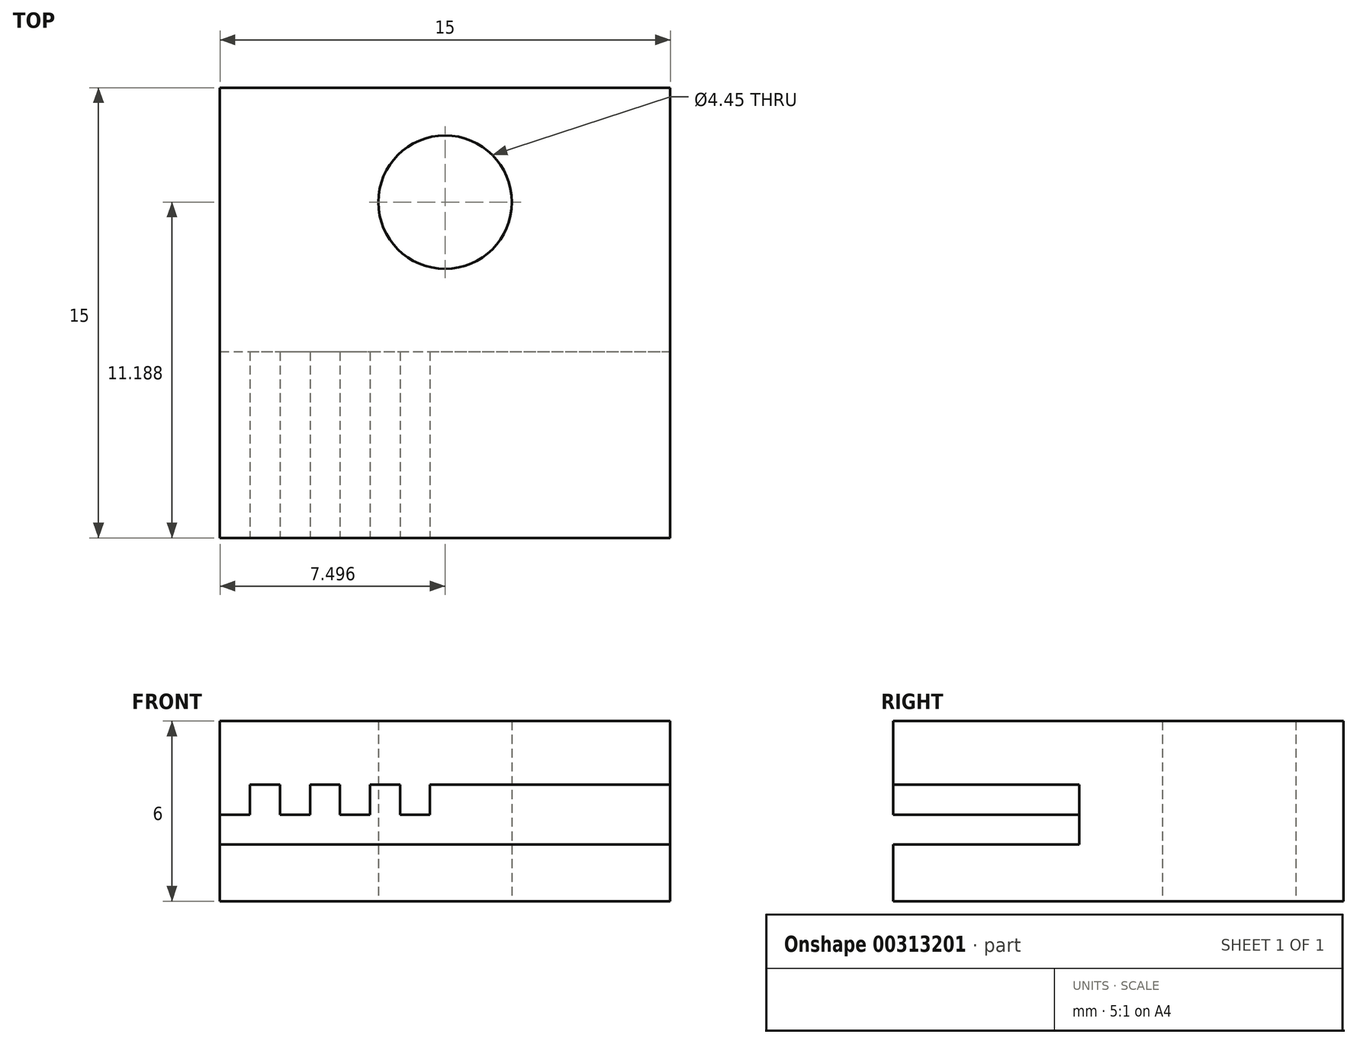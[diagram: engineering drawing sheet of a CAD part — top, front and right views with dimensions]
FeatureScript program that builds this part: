
annotation { "Feature Type Name" : "Feature", "Feature Type Description" : "" }
export const myFeature = defineFeature(function(context is Context, id is Id, definition is map)
    precondition{}
    {
        {
            var Q0;
            Q0=qCreatedBy(makeId("Top.planeOp"),FACE);
            var sketch = newSketch(context, id + "F0", { "sketchPlane" : qUnion([Q0])});
            skLineSegment(sketch, "E0.bottom", {"start": v(6.14, 10.11) * mm, "end": v(21.14, 10.11) * mm});
            skLineSegment(sketch, "E0.top", {"start": v(6.14, -4.89) * mm, "end": v(21.14, -4.89) * mm});
            skLineSegment(sketch, "E0.left", {"start": v(6.14, 10.11) * mm, "end": v(6.14, -4.89) * mm});
            skLineSegment(sketch, "E0.right", {"start": v(21.14, 10.11) * mm, "end": v(21.14, -4.89) * mm});
            skSolve(sketch);
        }
        {
            var Q0;
            Q0=qSketchRegion(id+"F0",true);
            extrude(context, id + "F1", {"entities" : qUnion([Q0]), "depth" : 6 * mm});
        }
        {
            var Q0;
            Q0=makeQuery(id+"F1.opExtrude","SWEPT_FACE",FACE,{"disambiguationData":[OSD([sQuery(id+"F0.wireOp",EDGE,"E0.top")])]});
            var sketch = newSketch(context, id + "F2", { "sketchPlane" : qUnion([Q0])});
            skLineSegment(sketch, "E1", {"start": v(6.14, 1.88) * mm, "end": v(21.14, 1.88) * mm});
            skLineSegment(sketch, "E2", {"start": v(6.14, 2.88) * mm, "end": v(7.14, 2.88) * mm});
            skLineSegment(sketch, "E3", {"start": v(7.14, 2.88) * mm, "end": v(7.14, 3.88) * mm});
            skLineSegment(sketch, "E4", {"start": v(7.14, 3.88) * mm, "end": v(8.14, 3.88) * mm});
            skLineSegment(sketch, "E5", {"start": v(8.14, 3.88) * mm, "end": v(8.14, 2.88) * mm});
            skLineSegment(sketch, "E6.1.0.0", {"start": v(10.14, 3.88) * mm, "end": v(10.14, 2.88) * mm});
            skLineSegment(sketch, "E6.1.0.1", {"start": v(9.14, 3.88) * mm, "end": v(10.14, 3.88) * mm});
            skLineSegment(sketch, "E6.1.0.2", {"start": v(9.14, 2.88) * mm, "end": v(9.14, 3.88) * mm});
            skLineSegment(sketch, "E6.1.0.3", {"start": v(8.14, 2.88) * mm, "end": v(9.14, 2.88) * mm});
            skLineSegment(sketch, "E6.2.0.0", {"start": v(12.14, 3.88) * mm, "end": v(12.14, 2.88) * mm});
            skLineSegment(sketch, "E6.2.0.1", {"start": v(11.14, 3.88) * mm, "end": v(12.14, 3.88) * mm});
            skLineSegment(sketch, "E6.2.0.2", {"start": v(11.14, 2.88) * mm, "end": v(11.14, 3.88) * mm});
            skLineSegment(sketch, "E6.2.0.3", {"start": v(10.14, 2.88) * mm, "end": v(11.14, 2.88) * mm});
            skLineSegment(sketch, "E6.3.0.1", {"start": v(13.14, 3.88) * mm, "end": v(14.14, 3.88) * mm});
            skLineSegment(sketch, "E6.3.0.2", {"start": v(13.14, 2.88) * mm, "end": v(13.14, 3.88) * mm});
            skLineSegment(sketch, "E6.3.0.3", {"start": v(12.14, 2.88) * mm, "end": v(13.14, 2.88) * mm});
            skLineSegment(sketch, "E6.direction1", {"start": v(6.14, 2.88) * mm, "end": v(8.14, 2.88) * mm, "construction": true});
            skLineSegment(sketch, "E7", {"start": v(14.14, 3.88) * mm, "end": v(21.14, 3.88) * mm});
            skSolve(sketch);
        }
        {
            var Q0;
            {var subQ1=sQuery(id+"F2.wireOp",EDGE,"E1");Q0=makeQuery(id+"F2.imprint","IMPRINT",FACE,{"disambiguationData":[TD([[makeQuery(id+"F2.imprint","IMPRINT",EDGE,{"derivedFrom":subQ1}),1.0]])]});}
            extrude(context, id + "F3", {"entities" : qUnion([Q0]), "operationType" : NewBodyOperationType.REMOVE, "oppositeDirection" : true, "depth" : 6.2 * mm});
        }
        {
            var Q0;
            Q0=makeQuery(id+"F1.opExtrude","CAP_FACE",FACE,{"disambiguationData":[OSD([sQuery(id+"F0.wireOp",EDGE,"E0.bottom"),sQuery(id+"F0.wireOp",EDGE,"E0.top"),sQuery(id+"F0.wireOp",EDGE,"E0.left"),sQuery(id+"F0.wireOp",EDGE,"E0.right")])],"isStart":true});
            var sketch = newSketch(context, id + "F4", { "sketchPlane" : qUnion([Q0])});
            skCircle(sketch, "E8", {"center": v(13.64, -6.3) * mm, "radius": 2.22 * mm});
            skPoint(sketch, "E8.centerSnap0", {"position": v(13.64, -10.11) * mm});
            skSolve(sketch);
        }
        {
            var Q0;
            Q0=qSketchRegion(id+"F4",true);
            extrude(context, id + "F5", {"entities" : qUnion([Q0]), "operationType" : NewBodyOperationType.REMOVE, "oppositeDirection" : true, "depth" : 25 * mm});
        }
    });
